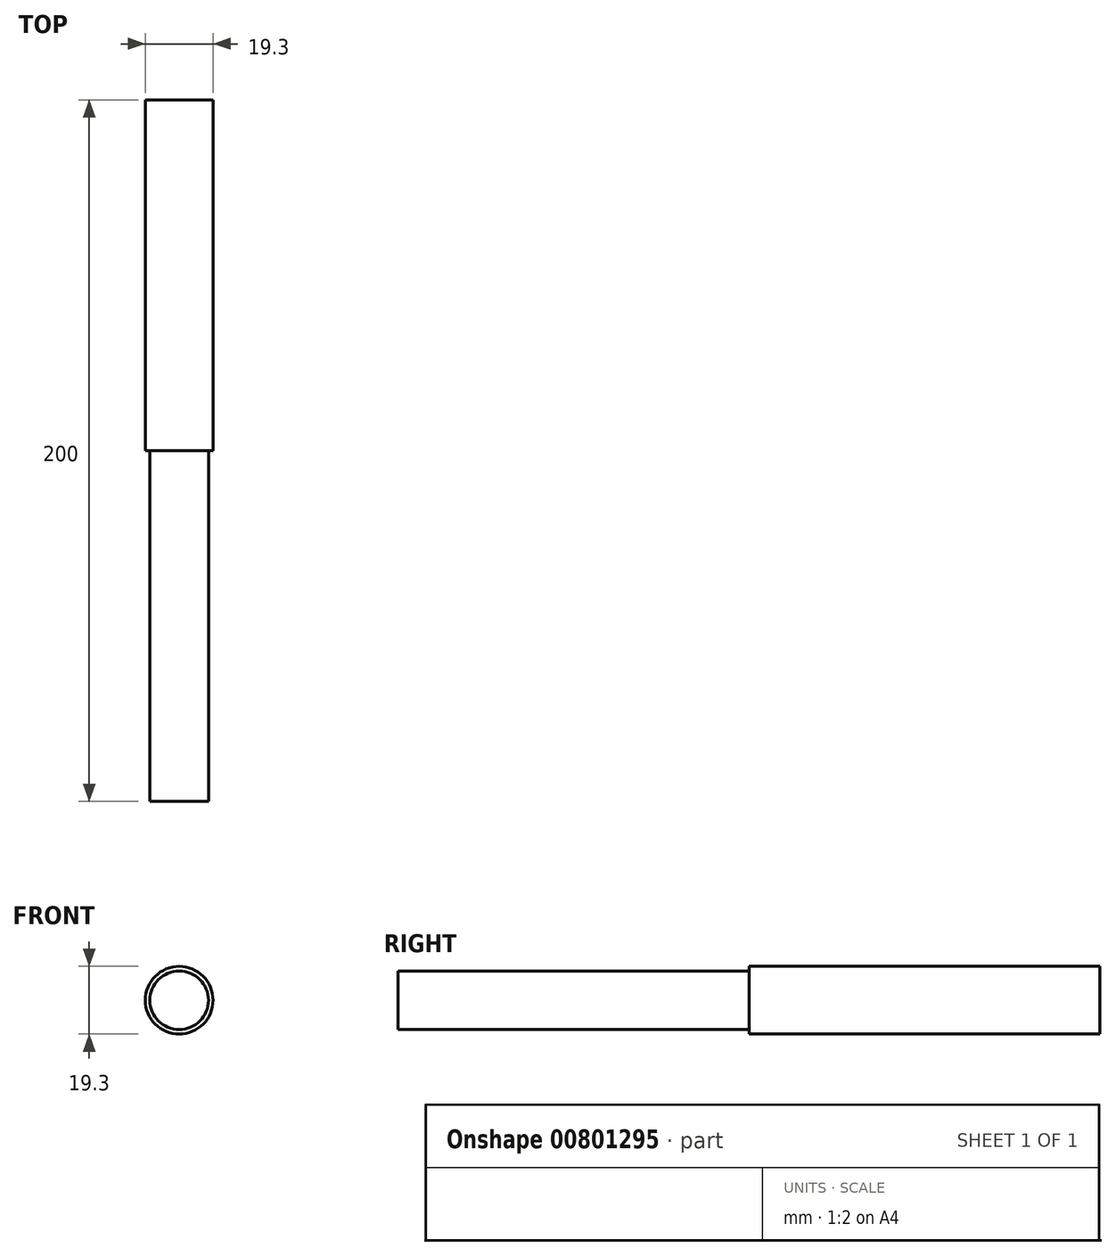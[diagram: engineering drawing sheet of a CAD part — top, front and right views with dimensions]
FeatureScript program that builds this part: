
annotation { "Feature Type Name" : "Feature", "Feature Type Description" : "" }
export const myFeature = defineFeature(function(context is Context, id is Id, definition is map)
    precondition{}
    {
        {
            var Q0;
            Q0=qCreatedBy(makeId("Front.planeOp"),FACE);
            var sketch = newSketch(context, id + "F0", { "sketchPlane" : qUnion([Q0])});
            skCircle(sketch, "E0", {"center": v(0, 0) * mm, "radius": 9.65 * mm});
            skCircle(sketch, "E1", {"center": v(0, 0) * mm, "radius": 8.35 * mm});
            skSolve(sketch);
        }
        {
            var Q0;
            Q0=makeQuery(id+"F0.imprint","IMPRINT",FACE,{"disambiguationData":[TD([[makeQuery(id+"F0.imprint","IMPRINT",EDGE,{"derivedFrom":sQuery(id+"F0.wireOp",EDGE,"E1")}),1.0]])]});
            var Q1;
            Q1=makeQuery(id+"F0.imprint","IMPRINT",FACE,{"disambiguationData":[TD([[makeQuery(id+"F0.imprint","IMPRINT",EDGE,{"derivedFrom":sQuery(id+"F0.wireOp",EDGE,"E0")}),1.0]])]});
            extrude(context, id + "F1", {"entities" : qUnion([Q0, Q1]), "oppositeDirection" : true, "depth" : 100 * mm, "offsetDistance" : 25 * mm});
        }
        {
            var Q0;
            Q0=makeQuery(id+"F0.imprint","IMPRINT",FACE,{"disambiguationData":[TD([[makeQuery(id+"F0.imprint","IMPRINT",EDGE,{"derivedFrom":sQuery(id+"F0.wireOp",EDGE,"E1")}),1.0]])]});
            extrude(context, id + "F2", {"entities" : qUnion([Q0]), "operationType" : NewBodyOperationType.ADD, "depth" : 100 * mm, "offsetDistance" : 25 * mm});
        }
    });
